# Revit family: Sanitary_Compound-Units_hansgrohe_54269XXX-Xilesa-E-Console_780-550_middle-cutout_countertop-basin-500-480_550-480
name_source: partatom
category: Furniture
units: mm (PartAtom-declared; Revit-internal decimal feet)

## family parameters
Cut with Voids When Loaded = No
Host = Face
OmniClass Number = 23.21.19.15.33.13
OmniClass Title = Residential Bathroom Specialty Casework
Render Appearance Source = Family Geometry
Room Calculation Point = No
Shared = No

## types (4) — shared parameters
Description = Xilesa E Console 780/550 with cutout middle for countertop basin ground 500/480 and 550/480
Manufacturer = Hansgrohe
Model = 54269XXX
Product Page URL = https://www.hansgrohe.com
Product data url = https://www.bimobject.com
URL = https://www.hansgrohe.com
Version = 1
zero-valued in all types: Default Elevation, Height

## per-type parameters (varying)
| type | Material 1 |
| 550 Cashmere Oak | Hansgrohe - MDF - 550 Cashmere Oak |
| 700 Matt White | Hansgrohe - MDF - 700 Matt White |
| 760 Slate Matt Grey | Hansgrohe - MDF - 760 Slate Matt Grey |
| 780 Sand Matt Beige | Hansgrohe - MDF - 780 Sand Matt Beige |

## geometry (parser evidence)
native form markers: Sweep x3
no freeform markers — native parametric forms only
